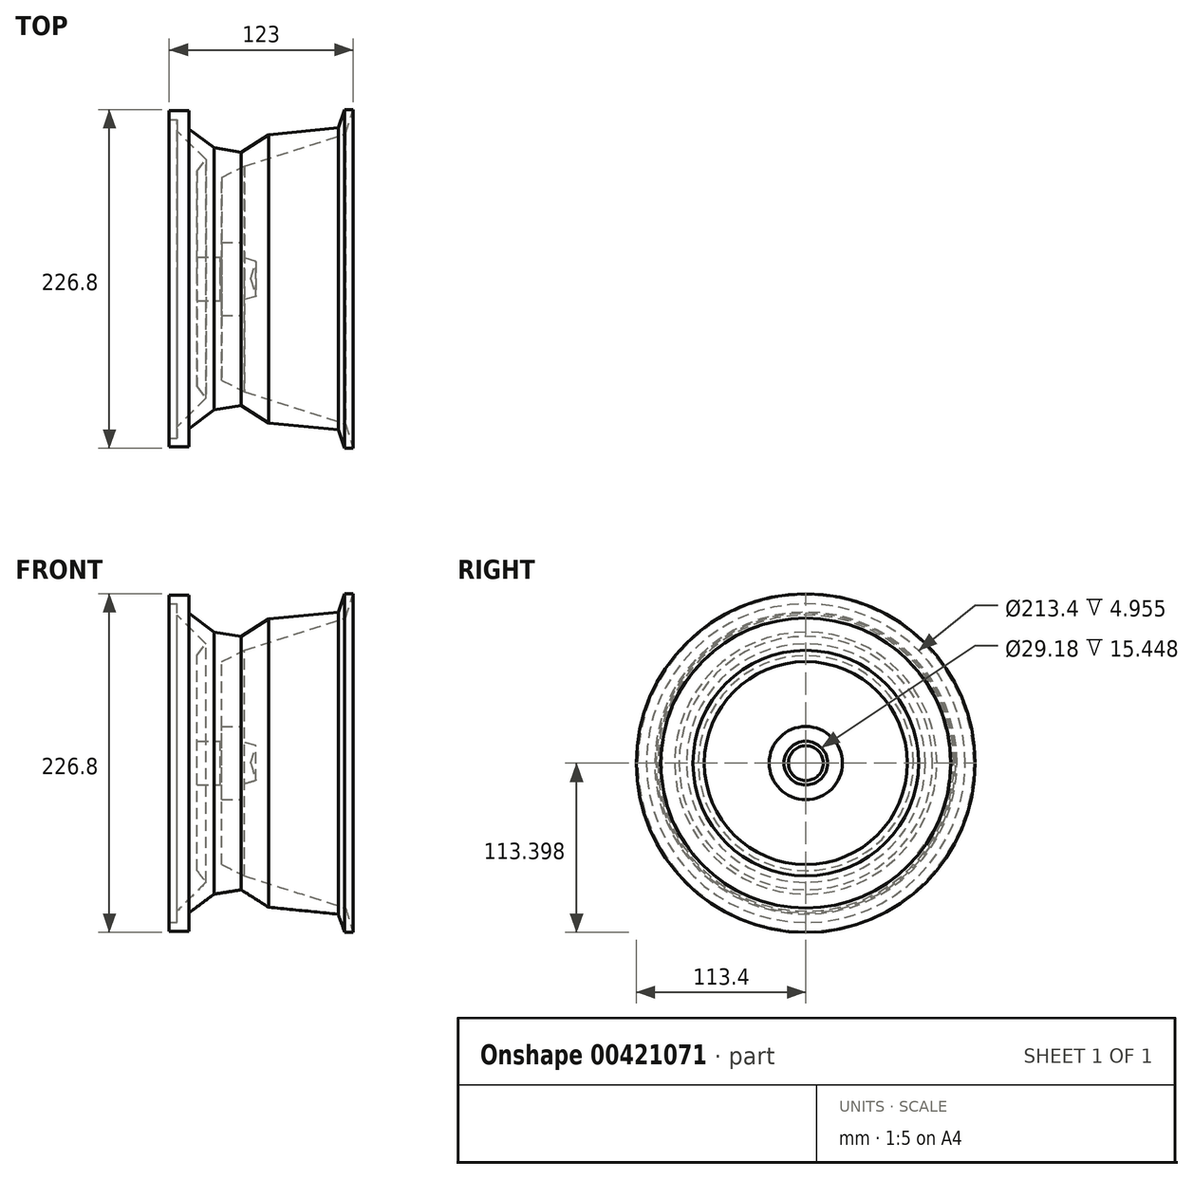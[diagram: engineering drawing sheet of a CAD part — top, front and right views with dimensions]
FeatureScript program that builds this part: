
annotation { "Feature Type Name" : "Feature", "Feature Type Description" : "" }
export const myFeature = defineFeature(function(context is Context, id is Id, definition is map)
    precondition{}
    {
        {
            var Q0;
            Q0=qCreatedBy(makeId("Front.planeOp"),FACE);
            var sketch = newSketch(context, id + "F0", { "sketchPlane" : qUnion([Q0])});
            skLineSegment(sketch, "E0", {"start": v(-39.35, 53.49) * mm, "end": v(-26.23, 53.49) * mm});
            skLineSegment(sketch, "E1", {"start": v(-26.23, 53.49) * mm, "end": v(-26.23, 41.24) * mm});
            skLineSegment(sketch, "E2", {"start": v(-26.23, 41.24) * mm, "end": v(-9.33, 28.71) * mm});
            skLineSegment(sketch, "E3", {"start": v(-9.33, 28.71) * mm, "end": v(8.74, 25.8) * mm});
            skLineSegment(sketch, "E4", {"start": v(8.74, 25.8) * mm, "end": v(27.1, 37.45) * mm});
            skLineSegment(sketch, "E5", {"start": v(27.1, 37.45) * mm, "end": v(73.74, 42.12) * mm});
            skLineSegment(sketch, "E6", {"start": v(73.74, 42.12) * mm, "end": v(78.12, 54.36) * mm});
            skLineSegment(sketch, "E7", {"start": v(78.12, 54.36) * mm, "end": v(83.65, 54.36) * mm});
            skLineSegment(sketch, "E8", {"start": v(83.65, 54.36) * mm, "end": v(78.7, 38.04) * mm});
            skLineSegment(sketch, "E9", {"start": v(78.7, 38.04) * mm, "end": v(11.08, 16.47) * mm});
            skLineSegment(sketch, "E10", {"start": v(11.08, 16.47) * mm, "end": v(-4.37, 8.9) * mm});
            skLineSegment(sketch, "E11", {"start": v(-4.37, 8.9) * mm, "end": v(-4.37, -34.54) * mm});
            skLineSegment(sketch, "E12", {"start": v(-4.37, -34.54) * mm, "end": v(8.74, -34.54) * mm});
            skLineSegment(sketch, "E13", {"start": v(8.74, -34.54) * mm, "end": v(8.74, -44.45) * mm});
            skLineSegment(sketch, "E14", {"start": v(8.74, -44.45) * mm, "end": v(18.65, -47.36) * mm});
            skLineSegment(sketch, "E15", {"start": v(18.65, -47.36) * mm, "end": v(15.22, -59.04) * mm});
            skLineSegment(sketch, "E16", {"start": v(15.22, -59.04) * mm, "end": v(-5.25, -59.04) * mm});
            skLineSegment(sketch, "E17", {"start": v(-5.25, -59.04) * mm, "end": v(-5.25, -44.45) * mm});
            skLineSegment(sketch, "E18", {"start": v(-5.25, -44.45) * mm, "end": v(-20.7, -44.45) * mm});
            skLineSegment(sketch, "E19", {"start": v(-20.7, -44.45) * mm, "end": v(-20.7, 12.97) * mm});
            skLineSegment(sketch, "E20", {"start": v(-20.7, 12.97) * mm, "end": v(-14.87, 20.84) * mm});
            skLineSegment(sketch, "E21", {"start": v(-14.87, 20.84) * mm, "end": v(-34.1, 40.08) * mm});
            skLineSegment(sketch, "E22", {"start": v(-34.1, 40.08) * mm, "end": v(-34.1, 47.66) * mm});
            skLineSegment(sketch, "E23", {"start": v(-34.1, 47.66) * mm, "end": v(-39.06, 47.66) * mm});
            skLineSegment(sketch, "E24", {"start": v(-39.06, 47.66) * mm, "end": v(-39.35, 53.49) * mm});
            skSolve(sketch);
        }
        {
            var Q0;
            Q0 = qSketchRegion(id + "F0", true);
            var Q1;
            Q1=sQuery(id+"F0.wireOp",EDGE,"E16");
            revolve(context, id + "F1", {"entities" : qUnion([Q0]), "axis" : qUnion([Q1]), "revolveType" : RevolveType.FULL});
        }
    });
